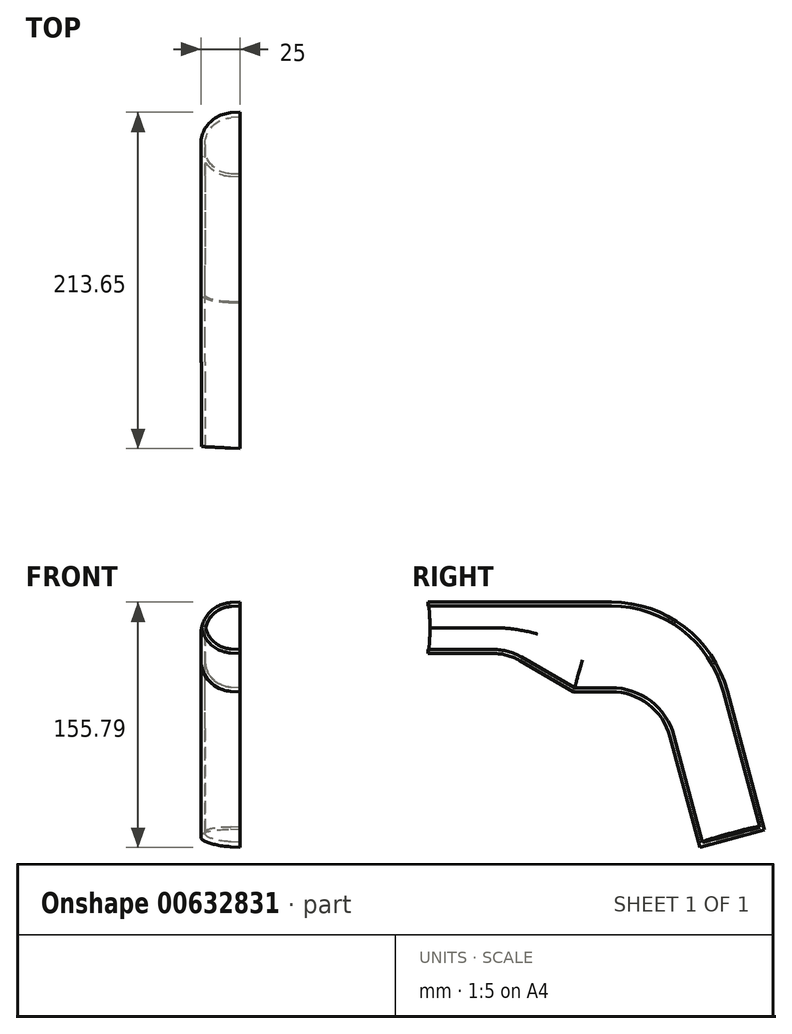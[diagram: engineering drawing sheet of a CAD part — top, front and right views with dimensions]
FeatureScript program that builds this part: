
annotation { "Feature Type Name" : "Feature", "Feature Type Description" : "" }
export const myFeature = defineFeature(function(context is Context, id is Id, definition is map)
    precondition{}
    {
        {
            var Q0;
            Q0=qCreatedBy(makeId("Right.planeOp"),FACE);
            var sketch = newSketch(context, id + "F0", { "sketchPlane" : qUnion([Q0])});
            skLineSegment(sketch, "E0", {"start": v(-115, 64.32) * mm, "end": v(-115, 94.32) * mm});
            skLineSegment(sketch, "E1", {"start": v(-115, 94.32) * mm, "end": v(0, 94.32) * mm});
            skArc(sketch, "E2", {"start": v(72.44, 38.73) * mm, "mid": v(45.66, 78.82) * mm, "end": v(0, 94.32) * mm});
            skLineSegment(sketch, "E3", {"start": v(72.44, 38.73) * mm, "end": v(95.74, -48.2) * mm});
            skLineSegment(sketch, "E4", {"start": v(95.74, -48.2) * mm, "end": v(57.1, -58.56) * mm});
            skLineSegment(sketch, "E5", {"start": v(57.1, -58.56) * mm, "end": v(38.64, 10.35) * mm});
            skArc(sketch, "E6", {"start": v(38.64, 10.35) * mm, "mid": v(24.35, 31.73) * mm, "end": v(0, 40) * mm});
            skLineSegment(sketch, "E7", {"start": v(0, 40) * mm, "end": v(-23.5, 40) * mm});
            skLineSegment(sketch, "E8", {"start": v(-23.5, 40) * mm, "end": v(-57.5, 59.63) * mm});
            skArc(sketch, "E9", {"start": v(-57.5, 59.63) * mm, "mid": v(-65.94, 63.13) * mm, "end": v(-75, 64.32) * mm});
            skLineSegment(sketch, "E10", {"start": v(-75, 64.32) * mm, "end": v(-115, 64.32) * mm});
            skSolve(sketch);
        }
        {
            var Q0;
            Q0=qSketchRegion(id+"F0",true);
            extrude(context, id + "F1", {"entities" : qUnion([Q0]), "depth" : 25 * mm, "offsetDistance" : 25 * mm, "hasDraft" : true, "draftAngle" : 3 * degree});
        }
        {
            var Q0;
            Q0=makeQuery(id+"F1.opExtrude","CAP_EDGE",EDGE,{"disambiguationData":[OSD([sQuery(id+"F0.wireOp",EDGE,"E2")])],"isStart":true});
            var Q1;
            Q1=makeQuery(id+"F1.opExtrude","CAP_EDGE",EDGE,{"disambiguationData":[OSD([sQuery(id+"F0.wireOp",EDGE,"E9")])],"isStart":true});
            var Q2;
            Q2=makeQuery(id+"F1.opExtrude","CAP_EDGE",EDGE,{"disambiguationData":[OSD([sQuery(id+"F0.wireOp",EDGE,"E10")])],"isStart":true});
            var Q3;
            Q3=makeQuery(id+"F1.opExtrude","CAP_EDGE",EDGE,{"disambiguationData":[OSD([sQuery(id+"F0.wireOp",EDGE,"E8")])],"isStart":true});
            var Q4;
            Q4=makeQuery(id+"F1.opExtrude","CAP_EDGE",EDGE,{"disambiguationData":[OSD([sQuery(id+"F0.wireOp",EDGE,"E7")])],"isStart":true});
            fillet(context, id + "F2", {"entities" : qUnion([Q0, Q1, Q2, Q3, Q4]), "radius" : 20 * mm, "tangentPropagation" : true, "allowEdgeOverflow" : false});
        }
        {
            var Q0;
            Q0=makeQuery(id+"F1.opExtrude","CAP_FACE",FACE,{"disambiguationData":[OSD([sQuery(id+"F0.wireOp",EDGE,"E0"),sQuery(id+"F0.wireOp",EDGE,"E1"),sQuery(id+"F0.wireOp",EDGE,"E2"),sQuery(id+"F0.wireOp",EDGE,"E3"),sQuery(id+"F0.wireOp",EDGE,"E4"),sQuery(id+"F0.wireOp",EDGE,"E5"),sQuery(id+"F0.wireOp",EDGE,"E6"),sQuery(id+"F0.wireOp",EDGE,"E7"),sQuery(id+"F0.wireOp",EDGE,"E8"),sQuery(id+"F0.wireOp",EDGE,"E9"),sQuery(id+"F0.wireOp",EDGE,"E10")])],"isStart":false});
            var Q1;
            Q1=makeQuery(id+"F1.opExtrude","SWEPT_FACE",FACE,{"disambiguationData":[OSD([sQuery(id+"F0.wireOp",EDGE,"E0")])]});
            shell(context, id + "F3", {"entities" : qUnion([Q0, Q1]), "thickness" : 2.5 * mm});
        }
    });
